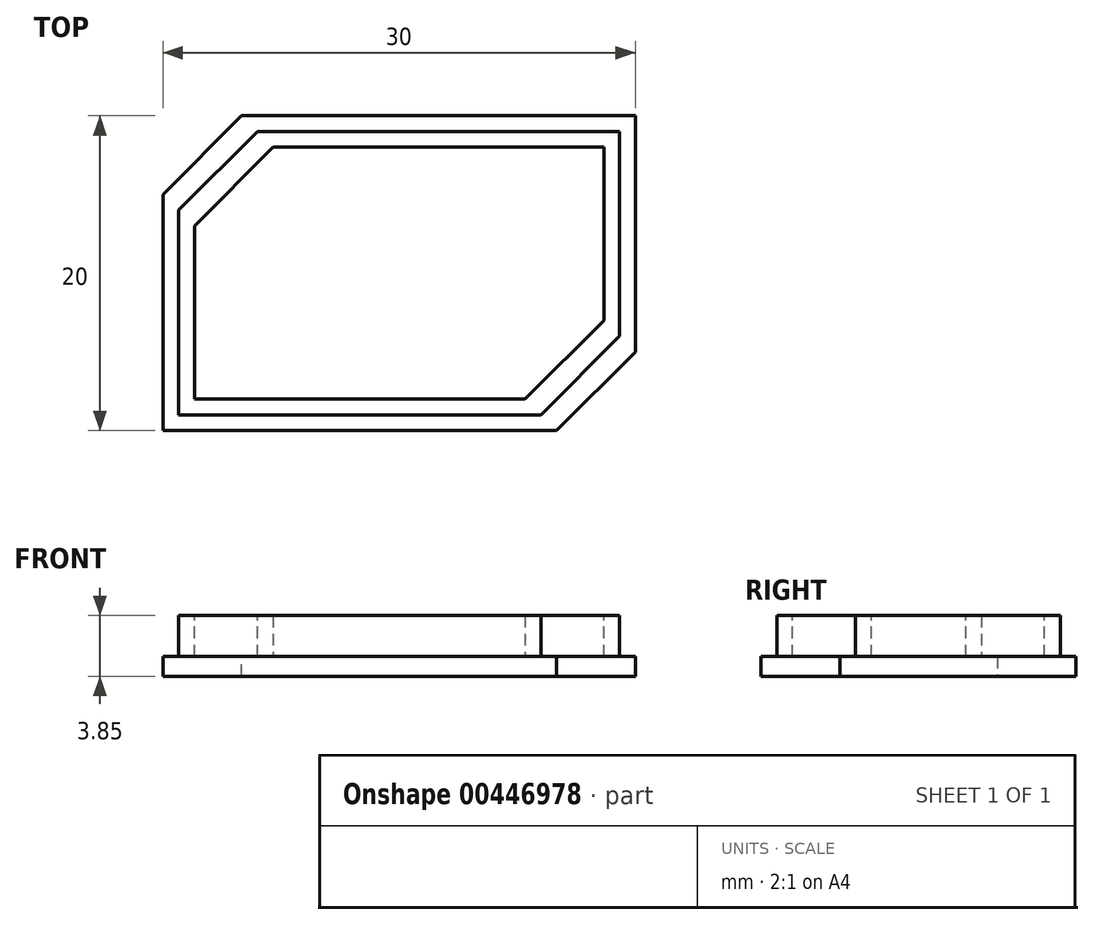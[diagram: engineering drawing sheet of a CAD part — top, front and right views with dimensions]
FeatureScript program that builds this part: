
annotation { "Feature Type Name" : "Feature", "Feature Type Description" : "" }
export const myFeature = defineFeature(function(context is Context, id is Id, definition is map)
    precondition{}
    {
        {
            var Q0;
            Q0=qCreatedBy(makeId("Top.planeOp"),FACE);
            var sketch = newSketch(context, id + "F0", { "sketchPlane" : qUnion([Q0])});
            skLineSegment(sketch, "E0.bottom", {"start": v(15, -10) * mm, "end": v(-15, -10) * mm});
            skLineSegment(sketch, "E0.top", {"start": v(15, 10) * mm, "end": v(-15, 10) * mm});
            skLineSegment(sketch, "E0.left", {"start": v(15, -10) * mm, "end": v(15, 10) * mm});
            skLineSegment(sketch, "E0.right", {"start": v(-15, -10) * mm, "end": v(-15, 10) * mm});
            skPoint(sketch, "E0.middle", {"position": v(0, 0) * mm});
            skSolve(sketch);
        }
        {
            var Q0;
            Q0=makeQuery(id+"F0.imprint","IMPRINT",FACE,{"disambiguationData":[TD([[makeQuery(id+"F0.imprint","IMPRINT",EDGE,{"derivedFrom":sQuery(id+"F0.wireOp",EDGE,"E0.bottom")}),-1.0]])]});
            extrude(context, id + "F1", {"entities" : qUnion([Q0]), "depth" : 1.25 * mm});
        }
        {
            var Q0;
            Q0=makeQuery(id+"F1.opExtrude","CAP_FACE",FACE,{"disambiguationData":[OSD([sQuery(id+"F0.wireOp",EDGE,"E0.bottom"),sQuery(id+"F0.wireOp",EDGE,"E0.top"),sQuery(id+"F0.wireOp",EDGE,"E0.left"),sQuery(id+"F0.wireOp",EDGE,"E0.right")])],"isStart":false});
            var sketch = newSketch(context, id + "F2", { "sketchPlane" : qUnion([Q0])});
            skLineSegment(sketch, "E1.bottom", {"start": v(14, -9) * mm, "end": v(-14, -9) * mm});
            skLineSegment(sketch, "E1.top", {"start": v(14, 9) * mm, "end": v(-14, 9) * mm});
            skLineSegment(sketch, "E1.left", {"start": v(14, -9) * mm, "end": v(14, 9) * mm});
            skLineSegment(sketch, "E1.right", {"start": v(-14, -9) * mm, "end": v(-14, 9) * mm});
            skPoint(sketch, "E1.middle", {"position": v(0, 0) * mm});
            skSolve(sketch);
        }
        {
            var Q0;
            Q0=makeQuery(id+"F2.imprint","IMPRINT",FACE,{"disambiguationData":[TD([[makeQuery(id+"F2.imprint","IMPRINT",EDGE,{"derivedFrom":sQuery(id+"F2.wireOp",EDGE,"E1.bottom")}),-1.0]])]});
            extrude(context, id + "F3", {"entities" : qUnion([Q0]), "operationType" : NewBodyOperationType.ADD, "depth" : 2.6 * mm});
        }
        {
            var Q0;
            Q0=makeQuery(id+"F3.opExtrude","CAP_FACE",FACE,{"disambiguationData":[OSD([sQuery(id+"F2.wireOp",EDGE,"E1.bottom"),sQuery(id+"F2.wireOp",EDGE,"E1.top"),sQuery(id+"F2.wireOp",EDGE,"E1.left"),sQuery(id+"F2.wireOp",EDGE,"E1.right")])],"isStart":false});
            var sketch = newSketch(context, id + "F4", { "sketchPlane" : qUnion([Q0])});
            skLineSegment(sketch, "E2.bottom", {"start": v(13, 8) * mm, "end": v(-13, 8) * mm});
            skLineSegment(sketch, "E2.top", {"start": v(13, -8) * mm, "end": v(-13, -8) * mm});
            skLineSegment(sketch, "E2.left", {"start": v(13, 8) * mm, "end": v(13, -8) * mm});
            skLineSegment(sketch, "E2.right", {"start": v(-13, 8) * mm, "end": v(-13, -8) * mm});
            skPoint(sketch, "E2.middle", {"position": v(0, 0) * mm});
            skSolve(sketch);
        }
        {
            var Q0;
            Q0=makeQuery(id+"F4.imprint","IMPRINT",FACE,{"disambiguationData":[TD([[makeQuery(id+"F4.imprint","IMPRINT",EDGE,{"derivedFrom":sQuery(id+"F4.wireOp",EDGE,"E2.bottom")}),1.0]])]});
            extrude(context, id + "F5", {"entities" : qUnion([Q0]), "operationType" : NewBodyOperationType.REMOVE, "oppositeDirection" : true, "depth" : 2.6 * mm});
        }
        {
            var Q0;
            Q0=makeQuery(id+"F5.boolean.opBoolean","COPY",EDGE,{"derivedFrom":makeQuery(id+"F5.opExtrude","SWEPT_EDGE",EDGE,{"disambiguationData":[OSD([sQuery(id+"F4.wireOp",EDGE,"E2.bottom"),sQuery(id+"F4.wireOp",EDGE,"E2.right")])]})});
            var Q1;
            Q1=makeQuery(id+"F5.boolean.opBoolean","COPY",EDGE,{"derivedFrom":makeQuery(id+"F5.opExtrude","SWEPT_EDGE",EDGE,{"disambiguationData":[OSD([sQuery(id+"F4.wireOp",EDGE,"E2.top"),sQuery(id+"F4.wireOp",EDGE,"E2.left")])]})});
            var Q2;
            Q2=makeQuery(id+"F3.opExtrude","SWEPT_EDGE",EDGE,{"disambiguationData":[OSD([sQuery(id+"F2.wireOp",EDGE,"E1.top"),sQuery(id+"F2.wireOp",EDGE,"E1.right")])]});
            var Q3;
            Q3=makeQuery(id+"F3.opExtrude","SWEPT_EDGE",EDGE,{"disambiguationData":[OSD([sQuery(id+"F2.wireOp",EDGE,"E1.bottom"),sQuery(id+"F2.wireOp",EDGE,"E1.left")])]});
            chamfer(context, id + "F6", {"entities" : qUnion([Q0, Q1, Q2, Q3]), "width" : 5 * mm, "tangentPropagation" : true});
        }
        {
            var Q0;
            Q0=makeQuery(id+"F1.opExtrude","SWEPT_EDGE",EDGE,{"disambiguationData":[OSD([sQuery(id+"F0.wireOp",EDGE,"E0.bottom"),sQuery(id+"F0.wireOp",EDGE,"E0.left")])]});
            var Q1;
            Q1=makeQuery(id+"F1.opExtrude","SWEPT_EDGE",EDGE,{"disambiguationData":[OSD([sQuery(id+"F0.wireOp",EDGE,"E0.top"),sQuery(id+"F0.wireOp",EDGE,"E0.right")])]});
            chamfer(context, id + "F7", {"entities" : qUnion([Q0, Q1]), "width" : 5 * mm, "tangentPropagation" : true});
        }
    });
